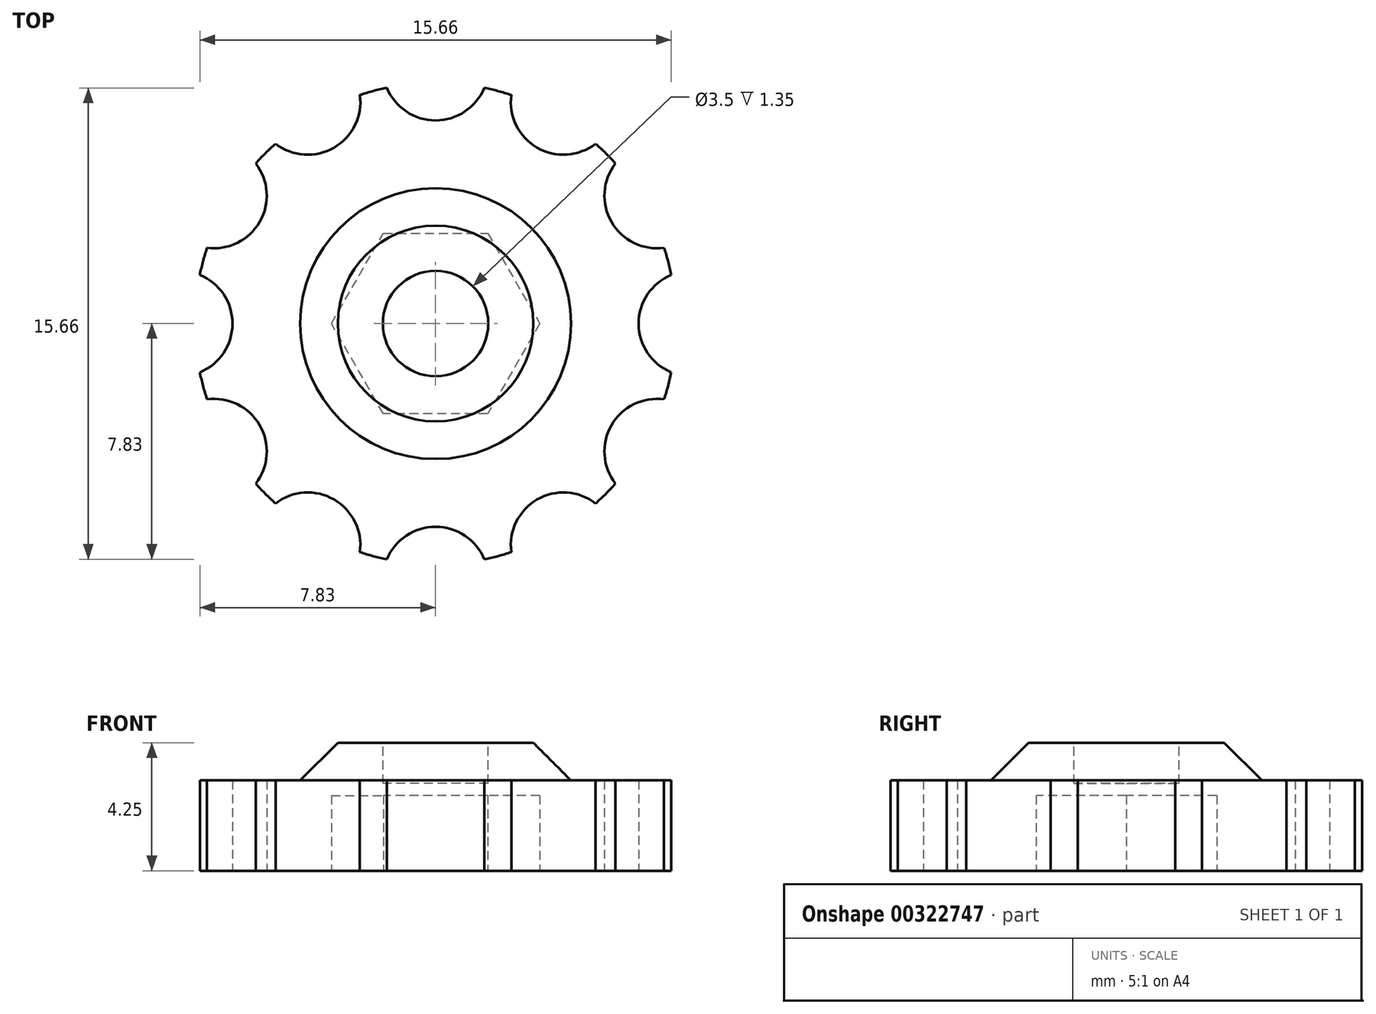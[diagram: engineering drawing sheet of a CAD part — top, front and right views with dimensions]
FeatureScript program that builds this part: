
annotation { "Feature Type Name" : "Feature", "Feature Type Description" : "" }
export const myFeature = defineFeature(function(context is Context, id is Id, definition is map)
    precondition{}
    {
        {
            var Q0;
            Q0=qCreatedBy(makeId("Top.planeOp"),FACE);
            var sketch = newSketch(context, id + "F0", { "sketchPlane" : qUnion([Q0])});
            skCircle(sketch, "E0.cCircle", {"center": v(0, 0) * mm, "radius": 3 * mm, "construction": true});
            skLineSegment(sketch, "E0.0", {"start": v(1.73, -3) * mm, "end": v(-1.73, -3) * mm});
            skLineSegment(sketch, "E0.1", {"start": v(-1.73, -3) * mm, "end": v(-3.46, 0) * mm});
            skLineSegment(sketch, "E0.2", {"start": v(-3.46, 0) * mm, "end": v(-1.73, 3) * mm});
            skLineSegment(sketch, "E0.3", {"start": v(-1.73, 3) * mm, "end": v(1.73, 3) * mm});
            skLineSegment(sketch, "E0.4", {"start": v(1.73, 3) * mm, "end": v(3.46, 0) * mm});
            skLineSegment(sketch, "E0.5", {"start": v(3.46, 0) * mm, "end": v(1.73, -3) * mm});
            skPoint(sketch, "E0.0.midPoint", {"position": v(0, -3) * mm});
            skCircle(sketch, "E1", {"center": v(0, 0) * mm, "radius": 8 * mm});
            skCircle(sketch, "E2", {"center": v(8.5, 0) * mm, "radius": 1.75 * mm});
            skCircle(sketch, "E3.1.0", {"center": v(7.36, 4.25) * mm, "radius": 1.75 * mm});
            skCircle(sketch, "E3.2.0", {"center": v(4.25, 7.36) * mm, "radius": 1.75 * mm});
            skCircle(sketch, "E3.3.0", {"center": v(0, 8.5) * mm, "radius": 1.75 * mm});
            skCircle(sketch, "E3.4.0", {"center": v(-4.25, 7.36) * mm, "radius": 1.75 * mm});
            skCircle(sketch, "E3.5.0", {"center": v(-7.36, 4.25) * mm, "radius": 1.75 * mm});
            skCircle(sketch, "E3.6.0", {"center": v(-8.5, 0) * mm, "radius": 1.75 * mm});
            skCircle(sketch, "E3.7.0", {"center": v(-7.36, -4.25) * mm, "radius": 1.75 * mm});
            skCircle(sketch, "E3.8.0", {"center": v(-4.25, -7.36) * mm, "radius": 1.75 * mm});
            skCircle(sketch, "E3.9.0", {"center": v(0, -8.5) * mm, "radius": 1.75 * mm});
            skCircle(sketch, "E3.10.0", {"center": v(4.25, -7.36) * mm, "radius": 1.75 * mm});
            skCircle(sketch, "E3.11.0", {"center": v(7.36, -4.25) * mm, "radius": 1.75 * mm});
            skSolve(sketch);
        }
        {
            var Q0;
            Q0=makeQuery(id+"F0.imprint","IMPRINT",FACE,{"disambiguationData":[TD([[makeQuery(id+"F0.imprint","IMPRINT",EDGE,{"derivedFrom":sQuery(id+"F0.wireOp",EDGE,"E0.0")}),1.0]])]});
            var Q1;
            Q1=makeQuery(id+"F0.imprint","IMPRINT",FACE,{"disambiguationData":[TD([[makeQuery(id+"F0.imprint","IMPRINT",EDGE,{"derivedFrom":sQuery(id+"F0.wireOp",EDGE,"E0.0")}),-1.0]])]});
            extrude(context, id + "F1", {"entities" : qUnion([Q0, Q1]), "depth" : 3 * mm});
        }
        {
            var Q0;
            Q0=makeQuery(id+"F0.imprint","IMPRINT",FACE,{"disambiguationData":[TD([[makeQuery(id+"F0.imprint","IMPRINT",EDGE,{"derivedFrom":sQuery(id+"F0.wireOp",EDGE,"E0.0")}),-1.0]])]});
            extrude(context, id + "F2", {"entities" : qUnion([Q0]), "operationType" : NewBodyOperationType.REMOVE, "depth" : 2.5 * mm});
        }
        {
            var Q0;
            Q0=makeQuery(id+"F1.opExtrude","CAP_FACE",FACE,{"disambiguationData":[OSD([sQuery(id+"F0.wireOp",EDGE,"E1"),sQuery(id+"F0.wireOp",EDGE,"E2"),sQuery(id+"F0.wireOp",EDGE,"E3.1.0"),sQuery(id+"F0.wireOp",EDGE,"E3.2.0"),sQuery(id+"F0.wireOp",EDGE,"E3.3.0"),sQuery(id+"F0.wireOp",EDGE,"E3.4.0"),sQuery(id+"F0.wireOp",EDGE,"E3.5.0"),sQuery(id+"F0.wireOp",EDGE,"E3.6.0"),sQuery(id+"F0.wireOp",EDGE,"E3.7.0"),sQuery(id+"F0.wireOp",EDGE,"E3.8.0"),sQuery(id+"F0.wireOp",EDGE,"E3.9.0"),sQuery(id+"F0.wireOp",EDGE,"E3.10.0"),sQuery(id+"F0.wireOp",EDGE,"E3.11.0")])],"isStart":false});
            var sketch = newSketch(context, id + "F3", { "sketchPlane" : qUnion([Q0])});
            skCircle(sketch, "E4", {"center": v(0, 0) * mm, "radius": 4.5 * mm});
            skSolve(sketch);
        }
        {
            var Q0;
            Q0=makeQuery(id+"F3.imprint","IMPRINT",FACE,{"disambiguationData":[TD([[makeQuery(id+"F3.imprint","IMPRINT",EDGE,{"derivedFrom":sQuery(id+"F3.wireOp",EDGE,"E4")}),1.0]])]});
            extrude(context, id + "F4", {"entities" : qUnion([Q0]), "operationType" : NewBodyOperationType.ADD, "depth" : 1.25 * mm});
        }
        {
            var Q0;
            Q0=makeQuery(id+"F4.opExtrude","CAP_FACE",FACE,{"disambiguationData":[OSD([sQuery(id+"F3.wireOp",EDGE,"E4")])],"isStart":false});
            var sketch = newSketch(context, id + "F5", { "sketchPlane" : qUnion([Q0])});
            skCircle(sketch, "E5", {"center": v(0, 0) * mm, "radius": 1.75 * mm});
            skSolve(sketch);
        }
        {
            var Q0;
            Q0=makeQuery(id+"F4.opExtrude","CAP_EDGE",EDGE,{"disambiguationData":[OSD([sQuery(id+"F3.wireOp",EDGE,"E4")])],"isStart":false});
            chamfer(context, id + "F6", {"entities" : qUnion([Q0]), "width" : 1.25 * mm, "tangentPropagation" : true});
        }
        {
            var Q0;
            Q0=makeQuery(id+"F5.imprint","IMPRINT",FACE,{"disambiguationData":[TD([[makeQuery(id+"F5.imprint","IMPRINT",EDGE,{"derivedFrom":sQuery(id+"F5.wireOp",EDGE,"E5")}),1.0]])]});
            extrude(context, id + "F7", {"entities" : qUnion([Q0]), "operationType" : NewBodyOperationType.REMOVE, "oppositeDirection" : true, "depth" : (1.75 - 0.4) * mm});
        }
    });
